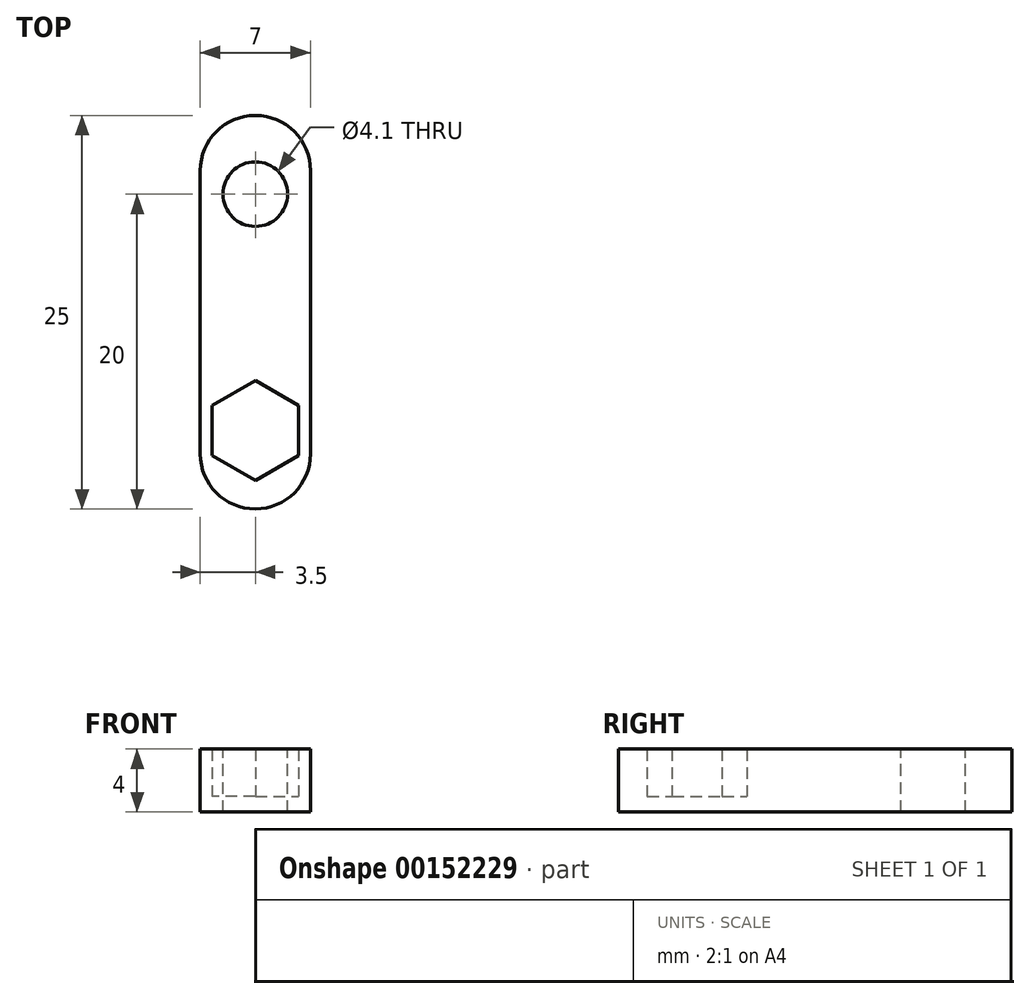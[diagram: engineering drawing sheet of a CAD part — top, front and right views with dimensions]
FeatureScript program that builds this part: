
annotation { "Feature Type Name" : "Feature", "Feature Type Description" : "" }
export const myFeature = defineFeature(function(context is Context, id is Id, definition is map)
    precondition{}
    {
        {
            var Q0;
            Q0=qCreatedBy(makeId("Top.planeOp"),FACE);
            var sketch = newSketch(context, id + "F0", { "sketchPlane" : qUnion([Q0])});
            skLineSegment(sketch, "E0.bottom", {"start": v(3.5, -20) * mm, "end": v(-3.5, -20) * mm});
            skLineSegment(sketch, "E0.top", {"start": v(3.5, 20) * mm, "end": v(-3.5, 20) * mm});
            skLineSegment(sketch, "E0.left", {"start": v(3.5, -20) * mm, "end": v(3.5, 20) * mm});
            skLineSegment(sketch, "E0.right", {"start": v(-3.5, -20) * mm, "end": v(-3.5, 20) * mm});
            skPoint(sketch, "E0.middle", {"position": v(0, 0) * mm});
            skCircle(sketch, "E1", {"center": v(0, 0) * mm, "radius": 2.05 * mm});
            skLineSegment(sketch, "E2", {"start": v(0, 0) * mm, "end": v(0, 5) * mm, "construction": true});
            skLineSegment(sketch, "E3", {"start": v(0, 5) * mm, "end": v(3.5, 5) * mm});
            skLineSegment(sketch, "E4", {"start": v(3.5, 5) * mm, "end": v(-3.5, 5) * mm});
            skLineSegment(sketch, "E5", {"start": v(0, -20) * mm, "end": v(0, -15) * mm, "construction": true});
            skCircle(sketch, "E6.cCircle", {"center": v(0, -15) * mm, "radius": 2.75 * mm, "construction": true});
            skLineSegment(sketch, "E6.0", {"start": v(-2.75, -16.59) * mm, "end": v(-2.75, -13.41) * mm});
            skLineSegment(sketch, "E6.1", {"start": v(-2.75, -13.41) * mm, "end": v(0, -11.82) * mm});
            skLineSegment(sketch, "E6.2", {"start": v(0, -11.82) * mm, "end": v(2.75, -13.41) * mm});
            skLineSegment(sketch, "E6.3", {"start": v(2.75, -13.41) * mm, "end": v(2.75, -16.59) * mm});
            skLineSegment(sketch, "E6.4", {"start": v(2.75, -16.59) * mm, "end": v(0, -18.18) * mm});
            skLineSegment(sketch, "E6.5", {"start": v(0, -18.18) * mm, "end": v(-2.75, -16.59) * mm});
            skPoint(sketch, "E6.0.midPoint", {"position": v(-2.75, -15) * mm});
            skSolve(sketch);
        }
        {
            var Q0;
            {var subQ2=sQuery(id+"F0.wireOp",EDGE,"E0.bottom");Q0=makeQuery(id+"F0.imprint","IMPRINT",FACE,{"disambiguationData":[TD([[makeQuery(id+"F0.imprint","IMPRINT",EDGE,{"derivedFrom":subQ2}),-1.0]])]});}
            var Q1;
            Q1=makeQuery(id+"F0.imprint","IMPRINT",FACE,{"disambiguationData":[TD([[makeQuery(id+"F0.imprint","IMPRINT",EDGE,{"derivedFrom":sQuery(id+"F0.wireOp",EDGE,"E6.0")}),-1.0]])]});
            extrude(context, id + "F1", {"entities" : qUnion([Q0, Q1]), "oppositeDirection" : true, "depth" : 1 * mm, "offsetDistance" : 25 * mm});
        }
        {
            var Q0;
            {var subQ2=sQuery(id+"F0.wireOp",EDGE,"E0.bottom");Q0=makeQuery(id+"F0.imprint","IMPRINT",FACE,{"disambiguationData":[TD([[makeQuery(id+"F0.imprint","IMPRINT",EDGE,{"derivedFrom":subQ2}),-1.0]])]});}
            extrude(context, id + "F2", {"entities" : qUnion([Q0]), "operationType" : NewBodyOperationType.ADD, "depth" : 3 * mm, "offsetDistance" : 25 * mm});
        }
        {
            var Q0;
            {var subQ0=sQuery(id+"F0.wireOp",EDGE,"E0.left");var subQ1=sQuery(id+"F0.wireOp",EDGE,"E0.bottom");Q0=makeQuery(id+"F2.boolean.opBoolean","MERGE",EDGE,{"derivedFrom":[makeQuery(id+"F1.opExtrude","SWEPT_EDGE",EDGE,{"disambiguationData":[OSD([subQ1,subQ0])]}),makeQuery(id+"F2.opExtrude","SWEPT_EDGE",EDGE,{"disambiguationData":[OSD([subQ1,subQ0])]})]});}
            var Q1;
            {var subQ0=sQuery(id+"F0.wireOp",EDGE,"E0.right");var subQ1=sQuery(id+"F0.wireOp",EDGE,"E0.bottom");Q1=makeQuery(id+"F2.boolean.opBoolean","MERGE",EDGE,{"derivedFrom":[makeQuery(id+"F1.opExtrude","SWEPT_EDGE",EDGE,{"disambiguationData":[OSD([subQ1,subQ0])]}),makeQuery(id+"F2.opExtrude","SWEPT_EDGE",EDGE,{"disambiguationData":[OSD([subQ1,subQ0])]})]});}
            var Q2;
            {var subQ0=sQuery(id+"F0.wireOp",EDGE,"E3");var subQ1=sQuery(id+"F0.wireOp",EDGE,"E0.left");Q2=makeQuery(id+"F2.boolean.opBoolean","MERGE",EDGE,{"derivedFrom":[makeQuery(id+"F1.opExtrude","SWEPT_EDGE",EDGE,{"disambiguationData":[OSD([subQ1,subQ0])]}),makeQuery(id+"F2.opExtrude","SWEPT_EDGE",EDGE,{"disambiguationData":[OSD([subQ1,subQ0])]})]});}
            var Q3;
            {var subQ0=sQuery(id+"F0.wireOp",EDGE,"E4");var subQ1=sQuery(id+"F0.wireOp",EDGE,"E0.right");Q3=makeQuery(id+"F2.boolean.opBoolean","MERGE",EDGE,{"derivedFrom":[makeQuery(id+"F1.opExtrude","SWEPT_EDGE",EDGE,{"disambiguationData":[OSD([subQ1,subQ0])]}),makeQuery(id+"F2.opExtrude","SWEPT_EDGE",EDGE,{"disambiguationData":[OSD([subQ1,subQ0])]})]});}
            fillet(context, id + "F3", {"entities" : qUnion([Q0, Q1, Q2, Q3]), "radius" : 3.5 * mm, "tangentPropagation" : true, "allowEdgeOverflow" : false});
        }
    });
